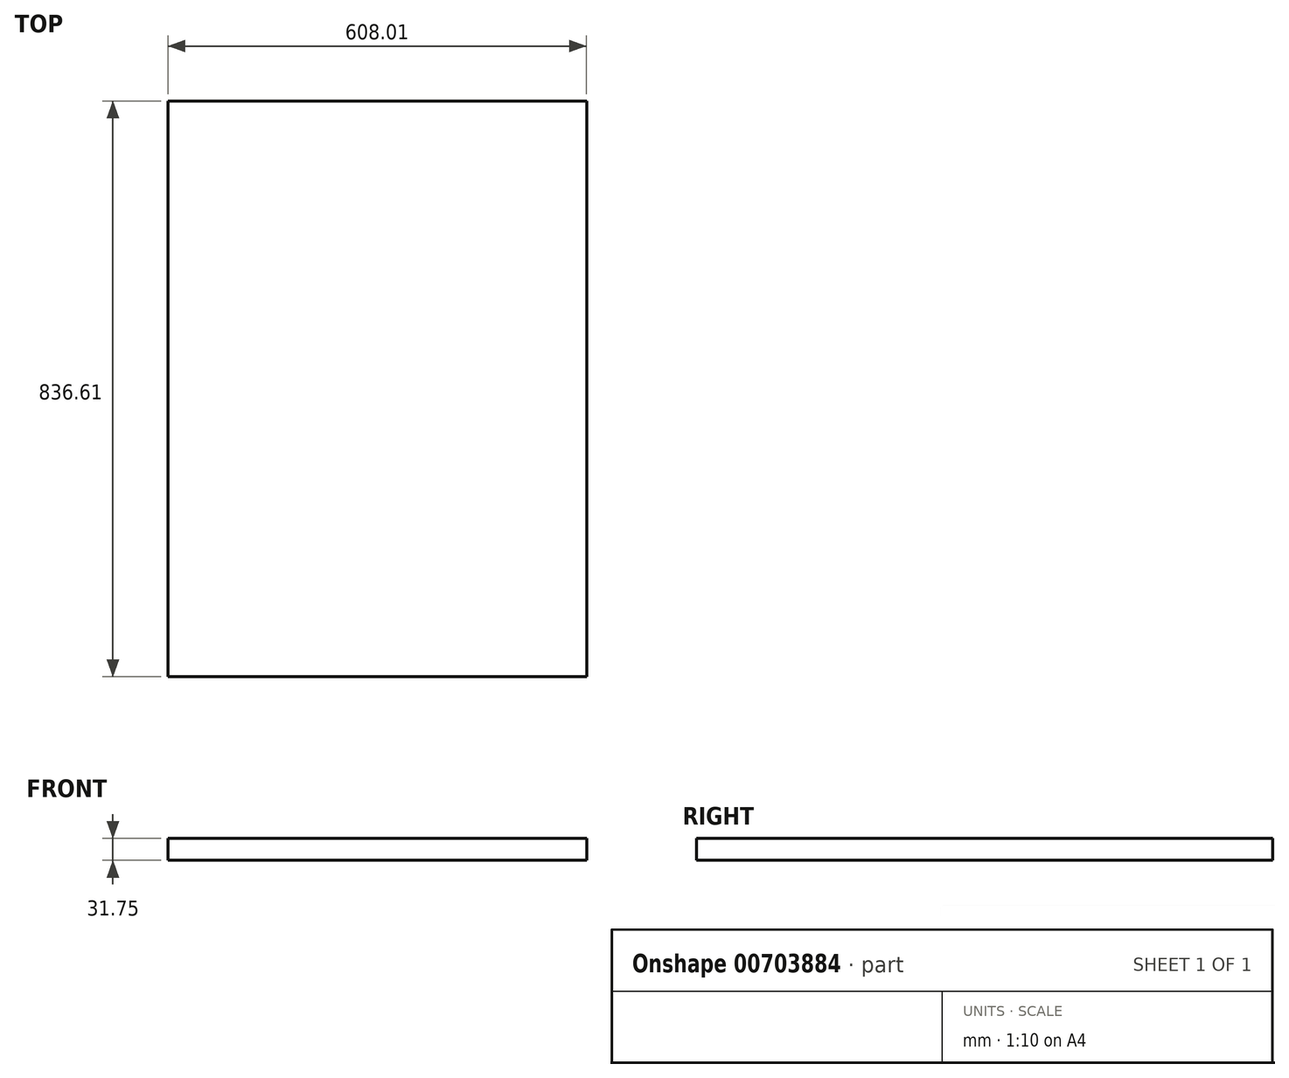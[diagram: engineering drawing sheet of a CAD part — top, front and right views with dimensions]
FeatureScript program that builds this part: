
annotation { "Feature Type Name" : "Feature", "Feature Type Description" : "" }
export const myFeature = defineFeature(function(context is Context, id is Id, definition is map)
    precondition{}
    {
        {
            var Q0;
            Q0=qCreatedBy(makeId("Front.planeOp"),FACE);
            var sketch = newSketch(context, id + "F0", { "sketchPlane" : qUnion([Q0])});
            skLineSegment(sketch, "E0.bottom", {"start": v(0, 0) * mm, "end": v(608.01, 0) * mm});
            skLineSegment(sketch, "E0.top", {"start": v(0, -31.75) * mm, "end": v(608.01, -31.75) * mm});
            skLineSegment(sketch, "E0.left", {"start": v(0, 0) * mm, "end": v(0, -31.75) * mm});
            skLineSegment(sketch, "E0.right", {"start": v(608.01, 0) * mm, "end": v(608.01, -31.75) * mm});
            skSolve(sketch);
        }
        {
            var Q0;
            Q0=qSketchRegion(id+"F0",true);
            extrude(context, id + "F1", {"entities" : qUnion([Q0]), "depth" : 836.6 * mm, "offsetDistance" : 25.4 * mm});
        }
    });
